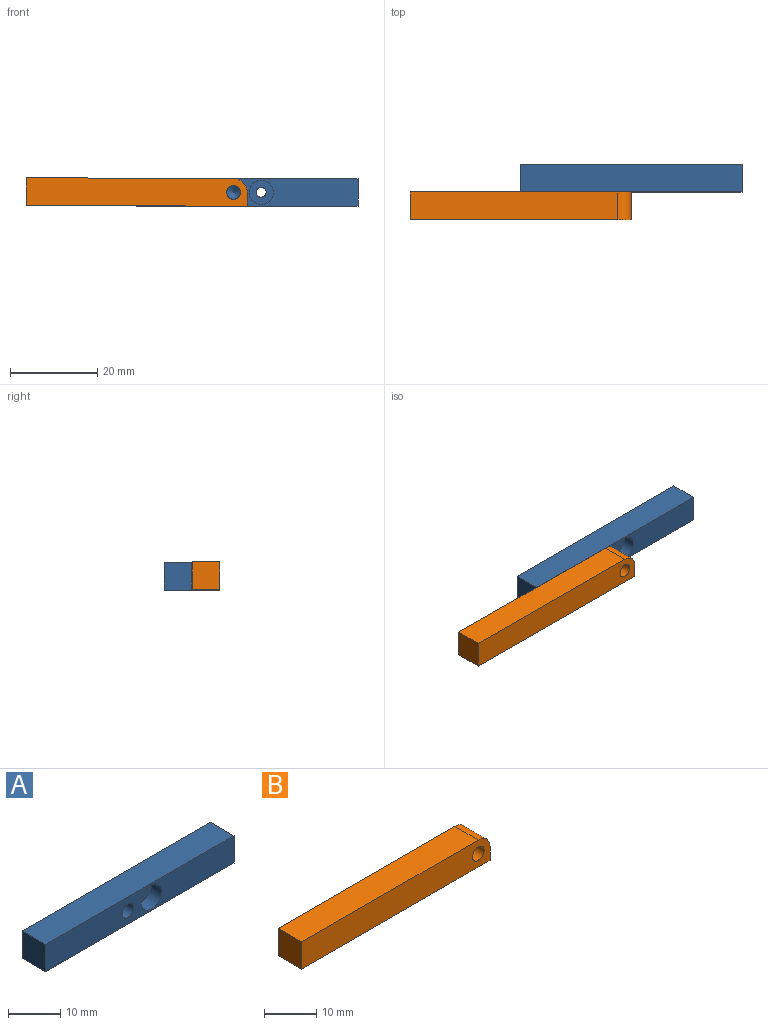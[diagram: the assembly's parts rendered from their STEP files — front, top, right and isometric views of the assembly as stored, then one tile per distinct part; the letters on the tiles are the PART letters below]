
ASSEMBLY  parts=2 mates=1
PART A: 11 faces, bbox 50.8x6.4x6.4 mm
  f0: plane 50.8x6.35mm, normal (0,0,1), area 322.6mm2, adj f1,f3,f4,f5
  f1: plane 6.35x6.35mm, normal (-1,0,0), area 40.3mm2, adj f0,f2,f4,f5
  f2: plane 50.8x6.35mm, normal (0,0,-1), area 322.6mm2, adj f1,f3,f4,f5
  f3: plane 6.35x6.35mm, normal (1,0,0), area 40.3mm2, adj f0,f2,f4,f5
  f4: plane 50.8x6.35mm, normal (0,1,0), area 318.6mm2, adj f0,f1,f2,f3,f8
  f5: plane 50.8x6.35mm, normal (0,-1,0), area 290.4mm2, adj f0,f1,f2,f3,f7,f10
  f6: cone r=0mm half-angle=59deg, axis (0,-1,0), area 9.2mm2, adj f7
  f7: cylinder r=1.59mm len=3.18mm, axis (0,-1,0), area 31.7mm2, adj f5,f6
  f8: cylinder r=1.13mm len=3.51mm, axis (0,-1,0), area 24.9mm2, adj f4,f9
  f9: plane 5.56x5.56mm, normal (0,-1,0), area 20.2mm2, adj f8,f10
  f10: cylinder r=2.78mm len=5.56mm, axis (0,-1,0), area 49.7mm2, adj f5,f9
PART B: 8 faces, bbox 50.8x6.4x6.4 mm
  f0: plane 6.35x6.35mm, normal (-1,0,0), area 40.3mm2, adj f1,f4,f5,f6
  f1: plane 50.8x6.35mm, normal (0,0,-1), area 322.6mm2, adj f0,f2,f5,f6
  f2: plane 6.35x3.18mm, normal (1,0,0), area 20.2mm2, adj f1,f3,f5,f6
  f3: cylinder r=3.17mm len=6.35mm, axis (0,1,0), area 31.7mm2, adj f2,f4,f5,f6
  f4: plane 47.63x6.35mm, normal (0,0,1), area 302.4mm2, adj f0,f3,f5,f6
  f5: plane 50.8x6.35mm, normal (0,-1,0), area 312.5mm2, adj f0,f1,f2,f3,f4,f7
  f6: plane 50.8x6.35mm, normal (0,1,0), area 312.5mm2, adj f0,f1,f2,f3,f4,f7
  f7: cylinder r=1.59mm len=6.35mm, axis (0,1,0), area 63.3mm2, adj f5,f6
PLACE A t=(-3.16,-11.89,-5.58)mm fixed
PLACE B rot(axis=(0,1,0),0.2deg) t=(-3.17,-11.89,-5.59)mm
MATE revolute A.f6 <-> B.f3  axis (0,-1,0) through (-6.33,-11.89,-2.4)mm
